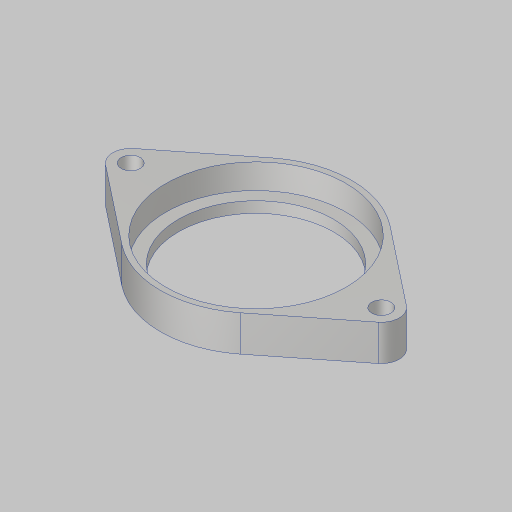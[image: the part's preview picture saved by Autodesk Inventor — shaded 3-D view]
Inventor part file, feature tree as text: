
AUTODESK INVENTOR PART (.ipt)
format: ipt  version: 2023.5 (Build 275446000, 446)  size: 125,440 bytes
history: native  units: in
note: dims shown in document units (in); Inventor stores cm internally (conversion verified against a paired STEP export)
features: sketch x2, extrude x2, hole x1
ambient origin geometry x8: Origin, YZ Plane, XZ Plane, XY Plane, X Axis, Y Axis, Z Axis, Center Point
bodies: Solid1 (feature_tree)
feature tree (5):
  sketch  "Sketch1"  dims[d0=1.875in d1=1.312in]
  extrude  "Extrusion1"  Depth=1.312in
  extrude  "Extrusion2"  Depth=1.0in
  hole  "Hole1"  [1 undecoded]
  sketch  "Sketch2"  dims[d2=0.375in d3=0.125in d4=0.0625in d5=0.375in d6=0.0in d7=1.885in d8=0.26in d9=0.0in d10=0.201in d11=0.75in d12=0.385in d13=0.25in d14=0.5635in d15=1.0in d16=0.8108in]
note: 1 required parameter value undecoded (feature->parameter linkage not recoverable at this tier; creation-order binding heuristic only, values carry confidence <= 0.55)
